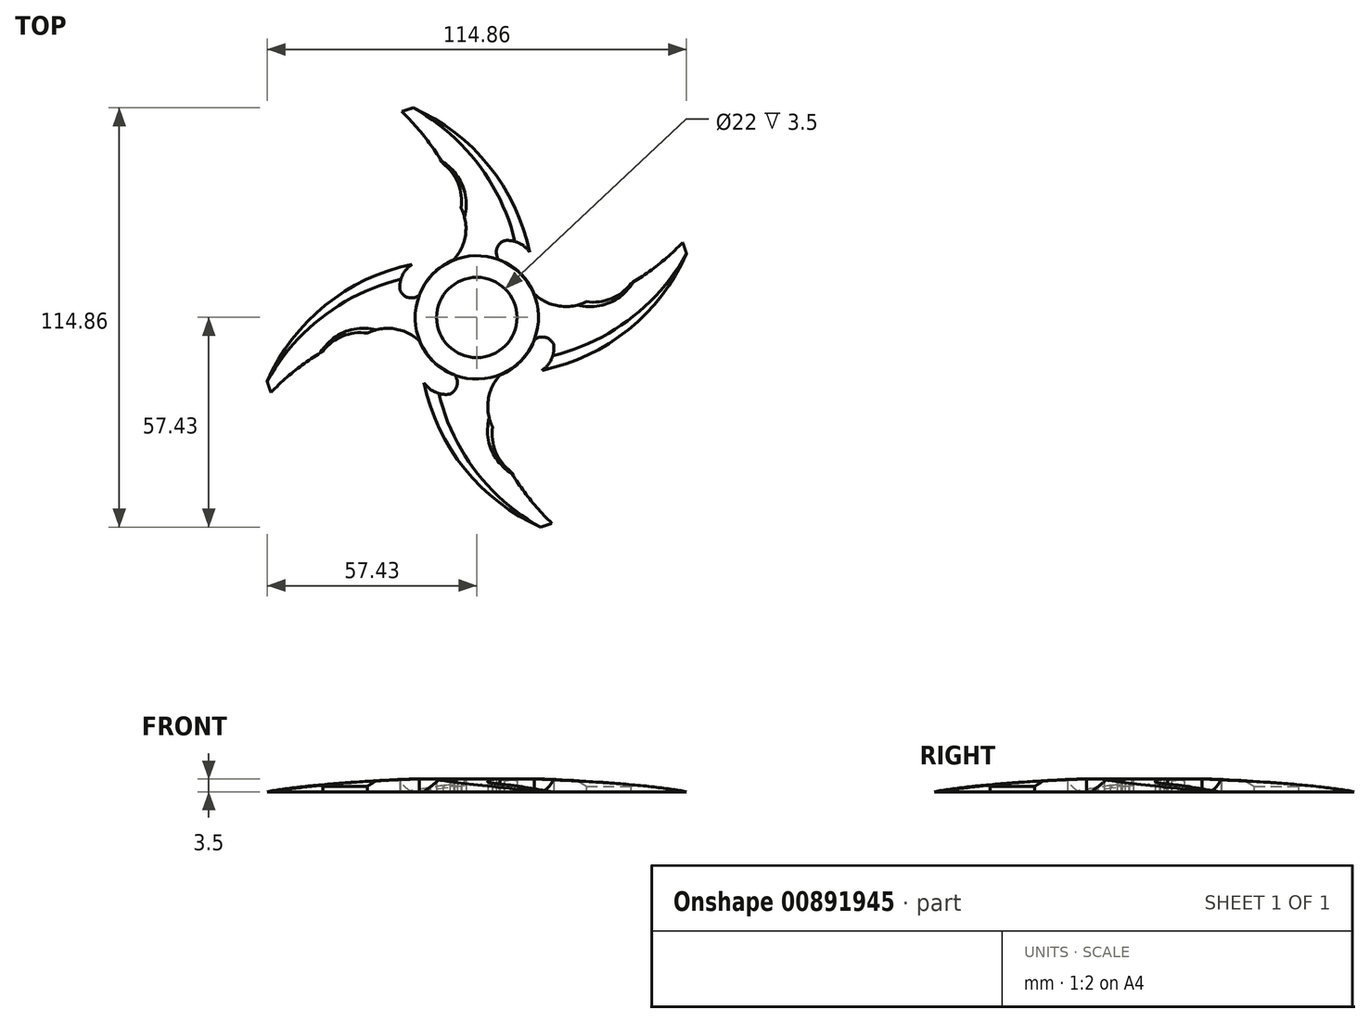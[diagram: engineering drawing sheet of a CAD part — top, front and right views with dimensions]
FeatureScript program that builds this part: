
annotation { "Feature Type Name" : "Feature", "Feature Type Description" : "" }
export const myFeature = defineFeature(function(context is Context, id is Id, definition is map)
    precondition{}
    {
        {
            var Q0;
            Q0=qCreatedBy(makeId("Top.planeOp"),FACE);
            var sketch = newSketch(context, id + "F0", { "sketchPlane" : qUnion([Q0])});
            skCircle(sketch, "E0", {"center": v(0, 0) * mm, "radius": 11 * mm});
            skArc(sketch, "E1", {"start": v(14.49, 17.85) * mm, "mid": v(0.82, 44.41) * mm, "end": v(-24.65, 60.03) * mm});
            skArc(sketch, "E2", {"start": v(14.49, 17.85) * mm, "mid": v(11.42, 20.45) * mm, "end": v(7.44, 21.03) * mm});
            skArc(sketch, "E3", {"start": v(7.44, 21.03) * mm, "mid": v(5.45, 18.74) * mm, "end": v(6.05, 15.77) * mm});
            skArc(sketch, "E4", {"start": v(-9.3, 42.19) * mm, "mid": v(-16.19, 51.78) * mm, "end": v(-24.65, 60.03) * mm});
            skArc(sketch, "E5", {"start": v(-4.32, 30.02) * mm, "mid": v(-5.13, 36.8) * mm, "end": v(-9.3, 42.19) * mm});
            skArc(sketch, "E6", {"start": v(-6.4, 15.77) * mm, "mid": v(-3.12, 22.57) * mm, "end": v(-4.32, 30.02) * mm});
            skArc(sketch, "E7.1.0", {"start": v(-30.02, -4.32) * mm, "mid": v(-36.8, -5.13) * mm, "end": v(-42.19, -9.3) * mm});
            skArc(sketch, "E7.1.1", {"start": v(-17.85, 14.49) * mm, "mid": v(-44.41, 0.82) * mm, "end": v(-60.03, -24.65) * mm});
            skArc(sketch, "E7.1.2", {"start": v(-42.19, -9.3) * mm, "mid": v(-51.78, -16.19) * mm, "end": v(-60.03, -24.65) * mm});
            skArc(sketch, "E7.1.3", {"start": v(-15.77, -6.4) * mm, "mid": v(-22.57, -3.12) * mm, "end": v(-30.02, -4.32) * mm});
            skArc(sketch, "E7.1.4", {"start": v(-21.03, 7.44) * mm, "mid": v(-18.74, 5.45) * mm, "end": v(-15.77, 6.05) * mm});
            skArc(sketch, "E7.1.5", {"start": v(-17.85, 14.49) * mm, "mid": v(-20.45, 11.42) * mm, "end": v(-21.03, 7.44) * mm});
            skArc(sketch, "E7.2.0", {"start": v(4.32, -30.02) * mm, "mid": v(5.13, -36.8) * mm, "end": v(9.3, -42.19) * mm});
            skArc(sketch, "E7.2.1", {"start": v(-14.49, -17.85) * mm, "mid": v(-0.82, -44.41) * mm, "end": v(24.65, -60.03) * mm});
            skArc(sketch, "E7.2.2", {"start": v(9.3, -42.19) * mm, "mid": v(16.19, -51.78) * mm, "end": v(24.65, -60.03) * mm});
            skArc(sketch, "E7.2.3", {"start": v(6.4, -15.77) * mm, "mid": v(3.12, -22.57) * mm, "end": v(4.32, -30.02) * mm});
            skArc(sketch, "E7.2.4", {"start": v(-7.44, -21.03) * mm, "mid": v(-5.45, -18.74) * mm, "end": v(-6.05, -15.77) * mm});
            skArc(sketch, "E7.2.5", {"start": v(-14.49, -17.85) * mm, "mid": v(-11.42, -20.45) * mm, "end": v(-7.44, -21.03) * mm});
            skArc(sketch, "E7.3.0", {"start": v(30.02, 4.32) * mm, "mid": v(36.8, 5.13) * mm, "end": v(42.19, 9.3) * mm});
            skArc(sketch, "E7.3.1", {"start": v(17.85, -14.49) * mm, "mid": v(44.41, -0.82) * mm, "end": v(60.03, 24.65) * mm});
            skArc(sketch, "E7.3.2", {"start": v(42.19, 9.3) * mm, "mid": v(51.78, 16.19) * mm, "end": v(60.03, 24.65) * mm});
            skArc(sketch, "E7.3.3", {"start": v(15.77, 6.4) * mm, "mid": v(22.57, 3.12) * mm, "end": v(30.02, 4.32) * mm});
            skArc(sketch, "E7.3.4", {"start": v(21.03, -7.44) * mm, "mid": v(18.74, -5.45) * mm, "end": v(15.77, -6.05) * mm});
            skArc(sketch, "E7.3.5", {"start": v(17.85, -14.49) * mm, "mid": v(20.45, -11.42) * mm, "end": v(21.03, -7.44) * mm});
            skArc(sketch, "E8", {"start": v(15.77, 6.4) * mm, "mid": v(11.91, 12.12) * mm, "end": v(6.05, 15.77) * mm});
            skArc(sketch, "E9.1.0", {"start": v(-6.4, 15.77) * mm, "mid": v(-12.12, 11.91) * mm, "end": v(-15.77, 6.05) * mm});
            skArc(sketch, "E9.2.0", {"start": v(-15.77, -6.4) * mm, "mid": v(-11.91, -12.12) * mm, "end": v(-6.05, -15.77) * mm});
            skArc(sketch, "E9.3.0", {"start": v(6.4, -15.77) * mm, "mid": v(12.12, -11.91) * mm, "end": v(15.77, -6.05) * mm});
            skSolve(sketch);
        }
        {
            var Q0;
            Q0 = qSketchRegion(id + "F0", true);
            extrude(context, id + "F1", {"entities" : qUnion([Q0]), "depth" : 7 * mm, "offsetDistance" : 25 * mm});
        }
        {
            var Q0;
            Q0=makeQuery(id+"F1.opExtrude","CAP_EDGE",EDGE,{"disambiguationData":[OSD([sQuery(id+"F0.wireOp",EDGE,"E1")])],"isStart":false});
            var Q1;
            Q1=makeQuery(id+"F1.opExtrude","CAP_EDGE",EDGE,{"disambiguationData":[OSD([sQuery(id+"F0.wireOp",EDGE,"E7.3.1")])],"isStart":false});
            var Q2;
            Q2=makeQuery(id+"F1.opExtrude","CAP_EDGE",EDGE,{"disambiguationData":[OSD([sQuery(id+"F0.wireOp",EDGE,"E7.2.1")])],"isStart":false});
            var Q3;
            Q3=makeQuery(id+"F1.opExtrude","CAP_EDGE",EDGE,{"disambiguationData":[OSD([sQuery(id+"F0.wireOp",EDGE,"E7.1.1")])],"isStart":false});
            var Q4;
            Q4=makeQuery(id+"F1.opExtrude","CAP_EDGE",EDGE,{"disambiguationData":[OSD([sQuery(id+"F0.wireOp",EDGE,"E7.3.1")])],"isStart":true});
            var Q5;
            Q5=makeQuery(id+"F1.opExtrude","CAP_EDGE",EDGE,{"disambiguationData":[OSD([sQuery(id+"F0.wireOp",EDGE,"E7.2.1")])],"isStart":true});
            var Q6;
            Q6=makeQuery(id+"F1.opExtrude","CAP_EDGE",EDGE,{"disambiguationData":[OSD([sQuery(id+"F0.wireOp",EDGE,"E1")])],"isStart":true});
            var Q7;
            Q7=makeQuery(id+"F1.opExtrude","CAP_EDGE",EDGE,{"disambiguationData":[OSD([sQuery(id+"F0.wireOp",EDGE,"E7.1.1")])],"isStart":true});
            chamfer(context, id + "F2", {"entities" : qUnion([Q0, Q1, Q2, Q3, Q4, Q5, Q6, Q7]), "width" : 3.5 * mm, "tangentPropagation" : true});
        }
        {
            var Q0;
            Q0=makeQuery(id+"F1.opExtrude","CAP_EDGE",EDGE,{"disambiguationData":[OSD([sQuery(id+"F0.wireOp",EDGE,"E7.1.0")])],"isStart":true});
            var Q1;
            Q1=makeQuery(id+"F1.opExtrude","CAP_EDGE",EDGE,{"disambiguationData":[OSD([sQuery(id+"F0.wireOp",EDGE,"E7.2.0")])],"isStart":true});
            var Q2;
            Q2=makeQuery(id+"F1.opExtrude","CAP_EDGE",EDGE,{"disambiguationData":[OSD([sQuery(id+"F0.wireOp",EDGE,"E7.3.0")])],"isStart":true});
            var Q3;
            Q3=makeQuery(id+"F1.opExtrude","CAP_EDGE",EDGE,{"disambiguationData":[OSD([sQuery(id+"F0.wireOp",EDGE,"E5")])],"isStart":true});
            var Q4;
            Q4=makeQuery(id+"F1.opExtrude","CAP_EDGE",EDGE,{"disambiguationData":[OSD([sQuery(id+"F0.wireOp",EDGE,"E5")])],"isStart":false});
            var Q5;
            Q5=makeQuery(id+"F1.opExtrude","CAP_EDGE",EDGE,{"disambiguationData":[OSD([sQuery(id+"F0.wireOp",EDGE,"E7.1.0")])],"isStart":false});
            var Q6;
            Q6=makeQuery(id+"F1.opExtrude","CAP_EDGE",EDGE,{"disambiguationData":[OSD([sQuery(id+"F0.wireOp",EDGE,"E7.2.0")])],"isStart":false});
            var Q7;
            Q7=makeQuery(id+"F1.opExtrude","CAP_EDGE",EDGE,{"disambiguationData":[OSD([sQuery(id+"F0.wireOp",EDGE,"E7.3.0")])],"isStart":false});
            chamfer(context, id + "F3", {"entities" : qUnion([Q0, Q1, Q2, Q3, Q4, Q5, Q6, Q7]), "width" : 2 * mm, "tangentPropagation" : true});
        }
        {
            var Q0;
            Q0=qCreatedBy(makeId("Front.planeOp"),FACE);
            var sketch = newSketch(context, id + "F4", { "sketchPlane" : qUnion([Q0])});
            skArc(sketch, "E10", {"start": v(60.03, 3.5) * mm, "mid": v(30.07, 6.35) * mm, "end": v(0, 7.3) * mm});
            skLineSegment(sketch, "E11", {"start": v(0, 3.5) * mm, "end": v(60.03, 3.5) * mm});
            skLineSegment(sketch, "E12", {"start": v(0, 0) * mm, "end": v(0, 7.3) * mm});
            skSolve(sketch);
        }
        {
            var Q0;
            Q0 = qSketchRegion(id + "F4", true);
            var Q1;
            Q1=sQuery(id+"F4.wireOp",EDGE,"E12");
            revolve(context, id + "F5", {"operationType" : NewBodyOperationType.INTERSECT, "surfaceOperationType" : NewSurfaceOperationType.NEW, "entities" : qUnion([Q0]), "axis" : qUnion([Q1]), "revolveType" : RevolveType.FULL, "oppositeDirection" : true});
        }
    });
